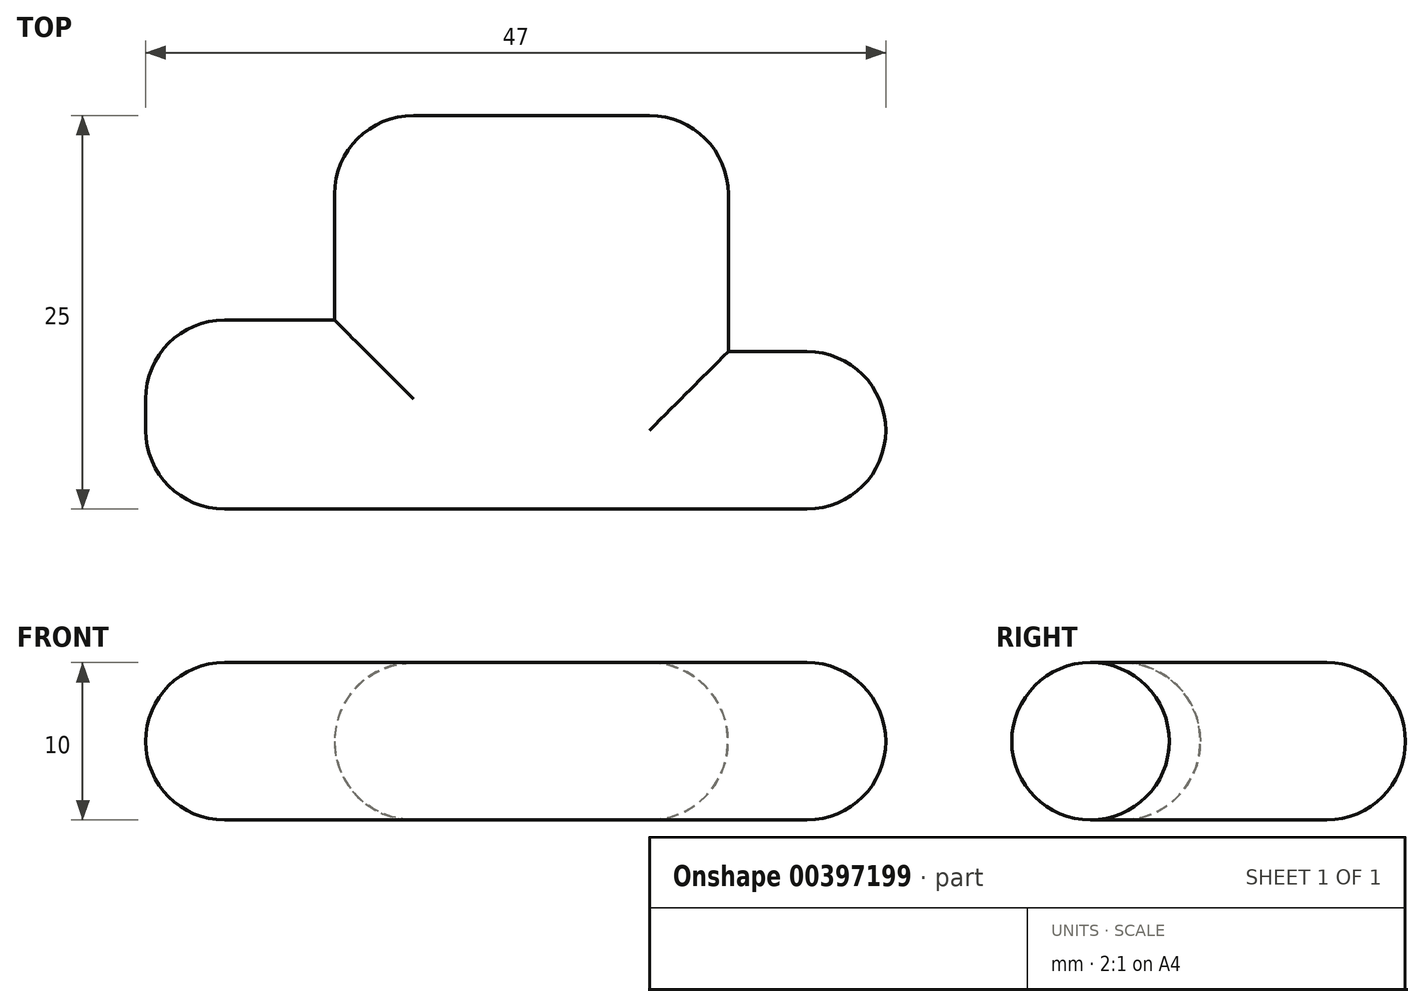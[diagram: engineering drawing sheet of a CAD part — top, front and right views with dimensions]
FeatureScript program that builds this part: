
annotation { "Feature Type Name" : "Feature", "Feature Type Description" : "" }
export const myFeature = defineFeature(function(context is Context, id is Id, definition is map)
    precondition{}
    {
        {
            var Q0;
            Q0=qCreatedBy(makeId("Top.planeOp"),FACE);
            var sketch = newSketch(context, id + "F0", { "sketchPlane" : qUnion([Q0])});
            skLineSegment(sketch, "E0.bottom", {"start": v(-22.47, 38.72) * mm, "end": v(2.53, 38.72) * mm});
            skLineSegment(sketch, "E0.top", {"start": v(-22.47, 13.72) * mm, "end": v(2.53, 13.72) * mm});
            skLineSegment(sketch, "E0.left", {"start": v(-22.47, 38.72) * mm, "end": v(-22.47, 13.72) * mm});
            skLineSegment(sketch, "E0.right", {"start": v(2.53, 38.72) * mm, "end": v(2.53, 13.72) * mm});
            skLineSegment(sketch, "E1.bottom", {"start": v(-34.47, 25.72) * mm, "end": v(-22.47, 25.72) * mm});
            skLineSegment(sketch, "E1.top", {"start": v(-34.47, 13.72) * mm, "end": v(-22.47, 13.72) * mm});
            skLineSegment(sketch, "E1.left", {"start": v(-34.47, 25.72) * mm, "end": v(-34.47, 13.72) * mm});
            skLineSegment(sketch, "E1.right", {"start": v(-22.47, 25.72) * mm, "end": v(-22.47, 13.72) * mm});
            skLineSegment(sketch, "E2.bottom", {"start": v(12.53, 23.72) * mm, "end": v(2.53, 23.72) * mm});
            skLineSegment(sketch, "E2.top", {"start": v(12.53, 13.72) * mm, "end": v(2.53, 13.72) * mm});
            skLineSegment(sketch, "E2.left", {"start": v(12.53, 23.72) * mm, "end": v(12.53, 13.72) * mm});
            skLineSegment(sketch, "E2.right", {"start": v(2.53, 23.72) * mm, "end": v(2.53, 13.72) * mm});
            skSolve(sketch);
        }
        {
            var Q0;
            Q0 = qSketchRegion(id + "F0", true);
            extrude(context, id + "F1", {"entities" : qUnion([Q0]), "depth" : 10 * mm});
        }
        {
            var Q0;
            Q0=makeQuery(id+"F1.opExtrude","SWEPT_EDGE",EDGE,{"disambiguationData":[OSD([sQuery(id+"F0.wireOp",EDGE,"E0.bottom"),sQuery(id+"F0.wireOp",EDGE,"E0.left")])]});
            var Q1;
            Q1=makeQuery(id+"F1.opExtrude","CAP_EDGE",EDGE,{"disambiguationData":[OSD([sQuery(id+"F0.wireOp",EDGE,"E0.left")])],"isStart":false});
            var Q2;
            Q2=makeQuery(id+"F1.opExtrude","CAP_EDGE",EDGE,{"disambiguationData":[OSD([sQuery(id+"F0.wireOp",EDGE,"E1.left")])],"isStart":false});
            var Q3;
            Q3=makeQuery(id+"F1.opExtrude","SWEPT_EDGE",EDGE,{"disambiguationData":[OSD([sQuery(id+"F0.wireOp",EDGE,"E1.bottom"),sQuery(id+"F0.wireOp",EDGE,"E1.left")])]});
            var Q4;
            Q4=makeQuery(id+"F1.opExtrude","SWEPT_FACE",FACE,{"disambiguationData":[OSD([sQuery(id+"F0.wireOp",EDGE,"E1.left")])]});
            var Q5;
            Q5=makeQuery(id+"F1.opExtrude","CAP_FACE",FACE,{"disambiguationData":[OSD([sQuery(id+"F0.wireOp",EDGE,"E0.bottom"),sQuery(id+"F0.wireOp",EDGE,"E0.top"),sQuery(id+"F0.wireOp",EDGE,"E0.left"),sQuery(id+"F0.wireOp",EDGE,"E0.right"),sQuery(id+"F0.wireOp",EDGE,"E1.bottom"),sQuery(id+"F0.wireOp",EDGE,"E1.top"),sQuery(id+"F0.wireOp",EDGE,"E1.left"),sQuery(id+"F0.wireOp",EDGE,"E2.bottom"),sQuery(id+"F0.wireOp",EDGE,"E2.top"),sQuery(id+"F0.wireOp",EDGE,"E2.left")])],"isStart":false});
            var Q6;
            Q6=makeQuery(id+"F1.opExtrude","SWEPT_FACE",FACE,{"disambiguationData":[OSD([sQuery(id+"F0.wireOp",EDGE,"E0.bottom")])]});
            var Q7;
            Q7=makeQuery(id+"F1.opExtrude","CAP_EDGE",EDGE,{"disambiguationData":[OSD([sQuery(id+"F0.wireOp",EDGE,"E2.bottom")])],"isStart":true});
            var Q8;
            Q8=makeQuery(id+"F1.opExtrude","CAP_FACE",FACE,{"disambiguationData":[OSD([sQuery(id+"F0.wireOp",EDGE,"E0.bottom"),sQuery(id+"F0.wireOp",EDGE,"E0.top"),sQuery(id+"F0.wireOp",EDGE,"E0.left"),sQuery(id+"F0.wireOp",EDGE,"E0.right"),sQuery(id+"F0.wireOp",EDGE,"E1.bottom"),sQuery(id+"F0.wireOp",EDGE,"E1.top"),sQuery(id+"F0.wireOp",EDGE,"E1.left"),sQuery(id+"F0.wireOp",EDGE,"E2.bottom"),sQuery(id+"F0.wireOp",EDGE,"E2.top"),sQuery(id+"F0.wireOp",EDGE,"E2.left")])],"isStart":true});
            var Q9;
            Q9=makeQuery(id+"F1.opExtrude","SWEPT_FACE",FACE,{"disambiguationData":[OSD([sQuery(id+"F0.wireOp",EDGE,"E2.left")])]});
            var Q10;
            Q10=makeQuery(id+"F1.opExtrude","SWEPT_FACE",FACE,{"disambiguationData":[OSD([sQuery(id+"F0.wireOp",EDGE,"E0.top"),sQuery(id+"F0.wireOp",EDGE,"E1.top"),sQuery(id+"F0.wireOp",EDGE,"E2.top")])]});
            fillet(context, id + "F2", {"entities" : qUnion([Q0, Q1, Q2, Q3, Q4, Q5, Q6, Q7, Q8, Q9, Q10]), "radius" : 5 * mm, "tangentPropagation" : true, "allowEdgeOverflow" : false});
        }
    });
